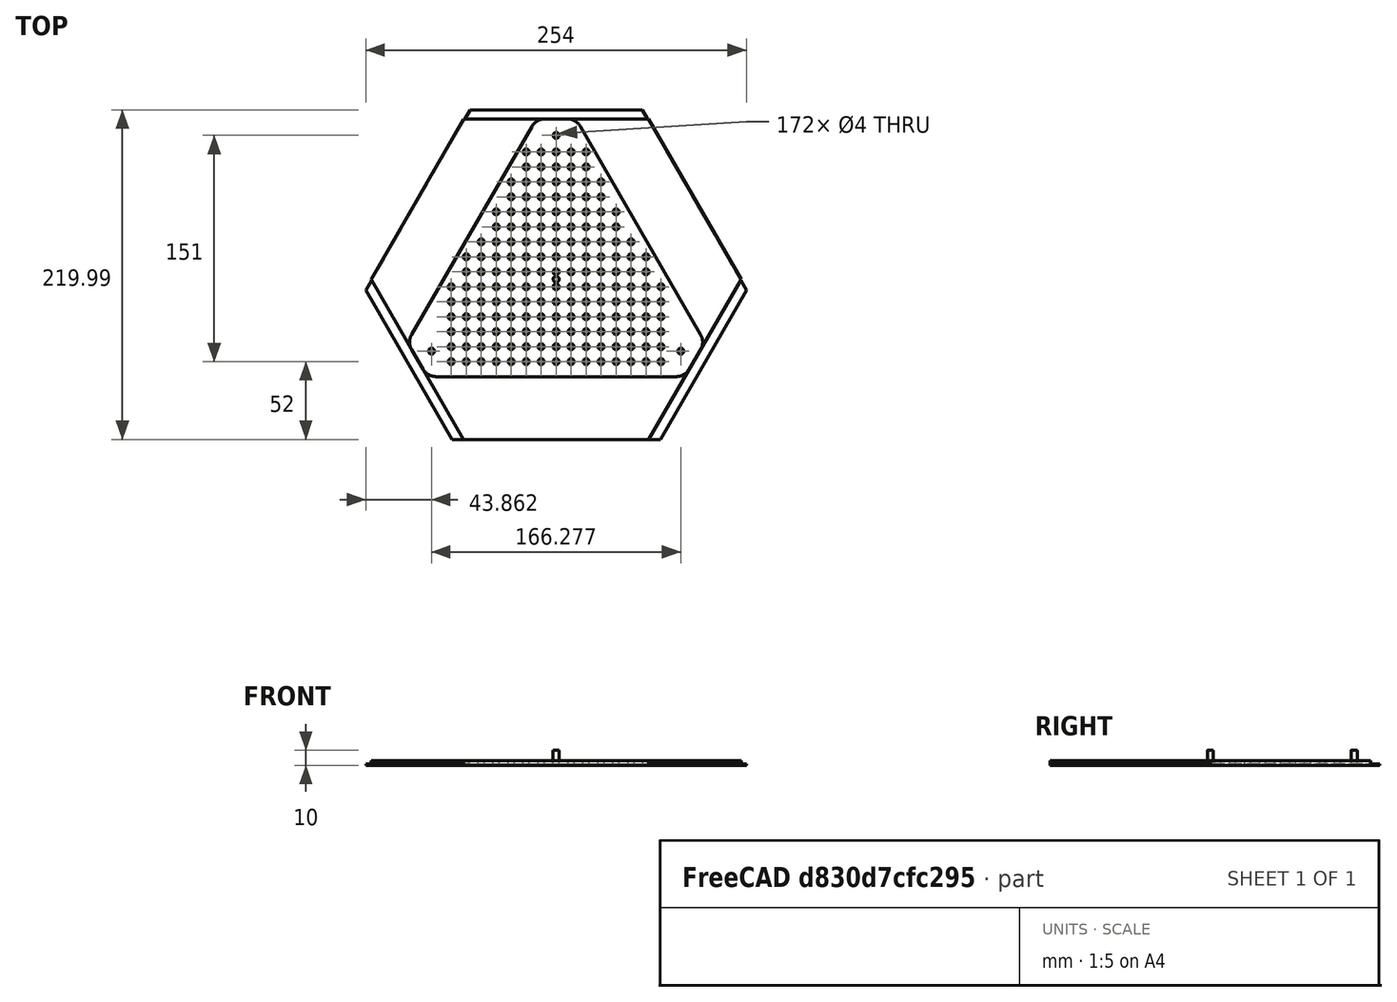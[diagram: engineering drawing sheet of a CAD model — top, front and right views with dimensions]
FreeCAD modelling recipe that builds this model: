
FCSTD DOCUMENT  (FreeCAD 0.19R)
Label: bottom
License: All rights reserved
LicenseURL: http://en.wikipedia.org/wiki/All_rights_reserved
objects: App::Part×3, Part::RegularPolygon×3, Part::Extrusion×3, Sketcher::SketchObject×2, PartDesign::Pad×2, PartDesign::Body×2, Part::MultiCommon×2, Part::Cylinder×2, Part::FeaturePython×2, Part::Cut×2, Part::MultiFuse×1, Part::Fillet×1
note: 22 computed .brp shape members not serialized (recipe doc carries the construction recipe); baked Part::Feature solids carry a one-line shape summary decoded from their .brp

FEATURE [Sketcher::SketchObject] Sketch
  FullyConstrained = false
  MapMode = 5
  Support = -> [XY_Plane001]
  sketch-geometry (8):
    g0: LineSegment StartX=-57.5 StartY=112.994 StartZ=0 EndX=-127 EndY=-7.38368 EndZ=0
    g1: LineSegment StartX=-69.5 StartY=-106.977 StartZ=0 EndX=69.5 EndY=-106.977 EndZ=0
    g2: LineSegment StartX=127 StartY=-7.38368 StartZ=0 EndX=57.5 EndY=112.994 EndZ=0
    g3: LineSegment StartX=-57.5 StartY=112.994 StartZ=0 EndX=57.5 EndY=112.994 EndZ=0
    g4: LineSegment StartX=-127 StartY=-7.38368 StartZ=0 EndX=-69.5 EndY=-106.977 EndZ=0
    g5: LineSegment StartX=127 StartY=-7.38368 StartZ=0 EndX=69.5 EndY=-106.977 EndZ=0
    g6: GeomPoint X=-0.001756 Y=-86.9766 Z=0
    g7: GeomPoint X=0 Y=-106.977 Z=0
  constraints (21):
    c: Symmetric(g0,g2,g-2)
    c: Symmetric(g2,g0,g-2)
    c: Symmetric(g1,g1,g-2)
    c: Equal(g1,g0)
    c: Angle(g0,g2) = 1.0472
    c: Distance(g0) = 139
    c: Coincident(g3,g0)
    c: Coincident(g3,g2)
    c: Coincident(g4,g0)
    c: Coincident(g4,g1)
    c: Coincident(g5,g2)
    c: Coincident(g5,g1)
    c: Equal(g5,g3)
    c: Distance(g5) = 115
    c: Distance(g2) = 139
    c: Distance(g1) = 139
    c: Distance(g4) = 115
    c: Distance(g3) = 115
    c: PointOnObject(g7,g1)
    c: PointOnObject(g7,g-2)
    c: DistanceY(g7,g6) = 20
FEATURE [PartDesign::Pad] Pad
  Direction = (1,1,1)
  Length = 1
  Length2 = 100
  Profile = -> Sketch
  Type = 0
FEATURE [PartDesign::Body] Body
  Group = -> [Sketch,Pad]
  Origin = -> Origin001
  Tip = -> Pad
FEATURE [App::Part] Part
  Group = -> [Body]
  Origin = -> Origin
FEATURE [App::Part] Part002  label="bottom part"
  Origin = -> Origin003
FEATURE [Part::RegularPolygon] RegularPolygon  label="body triangle"
  AttacherType = Attacher::AttachEngine3D
  Circumradius = 214
  Placement = pos=(0,0,0) rot=(0,0,1;0.523599rad)
  Polygon = 3
FEATURE [Part::RegularPolygon] RegularPolygon001  label="cut triangle"
  AttacherType = Attacher::AttachEngine3D
  Circumradius = 214
  Placement = pos=(0,0,0) rot=(0,0,-1;0.523599rad)
  Polygon = 3
FEATURE [Part::Extrusion] Extrude
  Base = -> RegularPolygon
  Dir = (0,0,1)
  DirMode = 2
  FaceMakerClass = Part::FaceMakerBullseye
  LengthFwd = 3
  LengthRev = 0
  Solid = true
  Symmetric = false
FEATURE [Part::Extrusion] Extrude001  label="Extrude with stepper"
  Base = -> RegularPolygon001
  Dir = (0,0,1)
  DirMode = 2
  FaceMakerClass = Part::FaceMakerBullseye
  LengthFwd = 3
  LengthRev = 0
  Solid = true
  Symmetric = false
FEATURE [Part::MultiCommon] Common  label="bottom plate common"
  Shapes = -> [Extrude,Extrude001]
FEATURE [Part::RegularPolygon] RegularPolygon002  label="cut triangle no stepper"
  AttacherType = Attacher::AttachEngine3D
  Circumradius = 130
  Placement = pos=(0,0,0) rot=(0,0,-1;0.523599rad)
  Polygon = 3
FEATURE [Part::Extrusion] Extrude002  label="Extrude no stepper"
  Base = -> RegularPolygon002
  Dir = (0,0,1)
  DirMode = 2
  FaceMakerClass = Part::FaceMakerBullseye
  LengthFwd = 3
  LengthRev = 0
  Solid = true
  Symmetric = false
FEATURE [Part::MultiCommon] Common001  label="bottom plate common smaller"
  Shapes = -> [Extrude002,Extrude]
FEATURE [Part::Cylinder] Cylinder  label="bolt hole"
  Angle = 360
  AttacherType = Attacher::AttachEngine3D
  Height = 10
  Placement = pos=(0,96,0) rot=(0,0,1;0rad)
  Radius = 2
FEATURE [Part::FeaturePython] Array  label="bolt hole array"  # Draft array (typed FeaturePython)
  Angle = 360
  ArrayType = 1
  Axis = (0,0,1)
  Base = -> Cylinder
  Center = (0,0,0)
  Count = 3
  ExpandArray = false
  Fuse = false
  IntervalAxis = (0,0,0)
  IntervalX = (50,0,0)
  IntervalY = (0,50,0)
  IntervalZ = (0,0,50)
  NumberCircles = 3
  NumberPolar = 3
  NumberX = 2
  NumberY = 2
  NumberZ = 1
  PlacementList = 3 placements: [(0,96,0),(-83.1384,-48,0),(83.1384,-48,0)]
  RadialDistance = 50
  ScaleList = (3) [(1,1,1),(1,1,1),(1,1,1)]
  Symmetry = 1
  TangentialDistance = 25
FEATURE [Part::Cylinder] Cylinder001  label="bolt hole001"
  Angle = 360
  AttacherType = Attacher::AttachEngine3D
  Height = 10
  Radius = 2
FEATURE [Part::FeaturePython] Array001  label="bolt hole matrix array"  # Draft array (typed FeaturePython)
  Angle = 360
  ArrayType = 0
  Axis = (0,0,1)
  Base = -> Cylinder001
  Center = (0,0,0)
  Count = 225
  ExpandArray = false
  Fuse = false
  IntervalAxis = (0,0,0)
  IntervalX = (10,0,0)
  IntervalY = (0,10,0)
  IntervalZ = (0,0,100)
  NumberCircles = 3
  NumberPolar = 5
  NumberX = 15
  NumberY = 15
  NumberZ = 1
  Placement = pos=(-70,-55,0) rot=(0,0,1;0rad)
  PlacementList = 225 placements: [(0,0,0),(0,10,0),(0,20,0),(0,30,0),(0,40,0),(0,50,0),(0,60,0),(0,70,0),(0,80,0),(0,90,0),(0,100,0),(0,110,0),(0,120,0),(0,130,0),(0,140,0),(10,0,0),(10,10,0),(10,20,0),(10,30,0),(10,40,0),(10,50,0),(10,60,0),(10,70,0),(10,80,0),(10,90,0),(10,100,0),(10,110,0),(10,120,0),(10,130,0),(10,140,0),(20,0,0),(20,10,0),(20,20,0),(20,30,0),(20,40,0),(20,50,0),(20,60,0),(20,70,0),(20,80,0),(20,90,0),+185 more]
  RadialDistance = 50
  ScaleList = (225) [(1,1,1),(1,1,1),(1,1,1),(1,1,1),(1,1,1),(1,1,1),(1,1,1),(1,1,1),(1,1,1),(1,1,1),(1,1,1),(1,1,1),(1,1,1),(1,1,1),(1,1,1),(1,1,1),(1,1,1),(1,1,1),+207 more]
  Symmetry = 1
  TangentialDistance = 25
FEATURE [Sketcher::SketchObject] Sketch001
  FullyConstrained = false
  MapMode = 5
  Support = -> [XY_Plane008]
  sketch-geometry (30):
    g0: LineSegment StartX=-87.1971 StartY=-15.976 StartZ=0 EndX=-81.3532 EndY=-8.96324 EndZ=0
    g1: LineSegment StartX=-81.3532 StartY=-8.96324 StartZ=0 EndX=-74.5702 EndY=-4.64335 EndZ=0
    g2: LineSegment StartX=-74.5702 StartY=-4.64335 StartZ=0 EndX=-62.263 EndY=10.1269 EndZ=0
    g3: LineSegment StartX=-62.263 StartY=10.1269 StartZ=0 EndX=-63.8214 EndY=15.5813 EndZ=0
    g4: LineSegment StartX=-63.8214 StartY=15.5813 StartZ=0 EndX=-54.0276 EndY=27.0886 EndZ=0
    g5: LineSegment StartX=-54.0276 StartY=27.0886 StartZ=0 EndX=-46.5193 EndY=30.4202 EndZ=0
    g6: LineSegment StartX=-46.5193 StartY=30.4202 StartZ=0 EndX=-44.3416 EndY=42.4633 EndZ=0
    g7: LineSegment StartX=-44.3416 StartY=42.4633 StartZ=0 EndX=-43.5624 EndY=49.0865 EndZ=0
    g8: LineSegment StartX=-43.5624 StartY=49.0865 StartZ=0 EndX=-34.6017 EndY=51.0344 EndZ=0
    g9: LineSegment StartX=-34.6017 StartY=51.0344 StartZ=0 EndX=-32.6538 EndY=66.6182 EndZ=0
    g10: LineSegment StartX=-32.6538 StartY=66.6182 StartZ=0 EndX=-25.4434 EndY=75.7274 EndZ=0
    g11: LineSegment StartX=-25.4434 StartY=75.7274 StartZ=0 EndX=-25.4434 EndY=86.4876 EndZ=0
    g12: LineSegment StartX=-25.4434 StartY=86.4876 StartZ=0 EndX=-10.0572 EndY=102.461 EndZ=0
    g13: LineSegment StartX=-10.0572 StartY=102.461 StartZ=0 EndX=12.5393 EndY=102.461 EndZ=0
    g14: LineSegment StartX=12.5393 StartY=102.461 StartZ=0 EndX=21.2703 EndY=88.8595 EndZ=0
    g15: LineSegment StartX=21.2703 StartY=88.8595 StartZ=0 EndX=23.6078 EndY=84.574 EndZ=0
    g16: LineSegment StartX=23.6078 StartY=84.574 StartZ=0 EndX=26.9543 EndY=77.1373 EndZ=0
    g17: LineSegment StartX=26.9543 StartY=77.1373 StartZ=0 EndX=26.1751 EndY=69.3454 EndZ=0
    g18: LineSegment StartX=26.1751 StartY=69.3454 StartZ=0 EndX=34.7462 EndY=68.9558 EndZ=0
    g19: LineSegment StartX=34.7462 StartY=68.9558 StartZ=0 EndX=36.6942 EndY=51.424 EndZ=0
    g20: LineSegment StartX=36.6942 StartY=51.424 StartZ=0 EndX=44.8757 EndY=47.9177 EndZ=0
    g21: LineSegment StartX=44.8757 StartY=47.9177 StartZ=0 EndX=45.8148 EndY=34.3162 EndZ=0
    g22: LineSegment StartX=45.8148 StartY=34.3162 StartZ=0 EndX=69.0306 EndY=11.2957 EndZ=0
    g23: LineSegment StartX=69.0306 StartY=11.2957 StartZ=0 EndX=65.9138 EndY=0 EndZ=0
    g24: LineSegment StartX=65.9138 StartY=0 StartZ=0 EndX=75.2641 EndY=-2.34012 EndZ=0
    g25: LineSegment StartX=75.2641 StartY=-2.34012 StartZ=0 EndX=76.8225 EndY=-21.0407 EndZ=0
    g26: LineSegment StartX=76.8225 StartY=-21.0407 StartZ=0 EndX=90.8479 EndY=-21.0407 EndZ=0
    g27: LineSegment StartX=90.8479 StartY=-21.0407 StartZ=0 EndX=102.925 EndY=117.655 EndZ=0
    g28: LineSegment StartX=102.925 StartY=117.655 StartZ=0 EndX=-102.002 EndY=117.655 EndZ=0
    g29: LineSegment StartX=-102.002 StartY=117.655 StartZ=0 EndX=-87.1971 EndY=-15.976 EndZ=0
  constraints (23):
    c: Coincident(g1,g0)
    c: Coincident(g6,g5)
    c: Coincident(g10,g9)
    c: Vertical(g11)
    c: Coincident(g13,g12)
    c: Horizontal(g13)
    c: Coincident(g15,g14)
    c: Coincident(g16,g15)
    c: Coincident(g17,g16)
    c: Coincident(g19,g18)
    c: Coincident(g21,g20)
    c: PointOnObject(g23,g-1)
    c: Coincident(g24,g23)
    c: Coincident(g25,g24)
    c: Horizontal(g26)
    c: Horizontal(g28)
    c: Coincident(g29,g28)
    c: Coincident(g29,g0)
    c: Coincident(g22,g21)
    c: Coincident(g5,g4)
    c: Coincident(g2,g1)
    c: Coincident(g10,g11)
    c: Coincident(g11,g12)
FEATURE [PartDesign::Pad] Pad001
  Direction = (1,1,1)
  Length = 100
  Length2 = 100
  Profile = -> Sketch001
  Type = 0
FEATURE [PartDesign::Body] Body004
  Group = -> [Sketch001,Pad001]
  Origin = -> Origin008
  Tip = -> Pad001
FEATURE [App::Part] Part003  label="bolt hole limit part"
  Group = -> [Body004]
  Origin = -> Origin007
FEATURE [Part::Cut] Cut001  label="bolt hole cut"
  Base = -> Array001
  Tool = -> Body004
FEATURE [Part::MultiFuse] Fusion  label="hole fusion"
  Shapes = -> [Array,Cut001]
FEATURE [Part::Fillet] Fillet  label="bottom plate common smaller fillet"
  Base = -> Common001
  Edges = 6 edges r=10: [Edge2,Edge4,Edge10,Edge16,Edge17,Edge18]
FEATURE [Part::Cut] Cut  label="bottom plate common smaller cut"
  Base = -> Fillet
  Tool = -> Fusion
